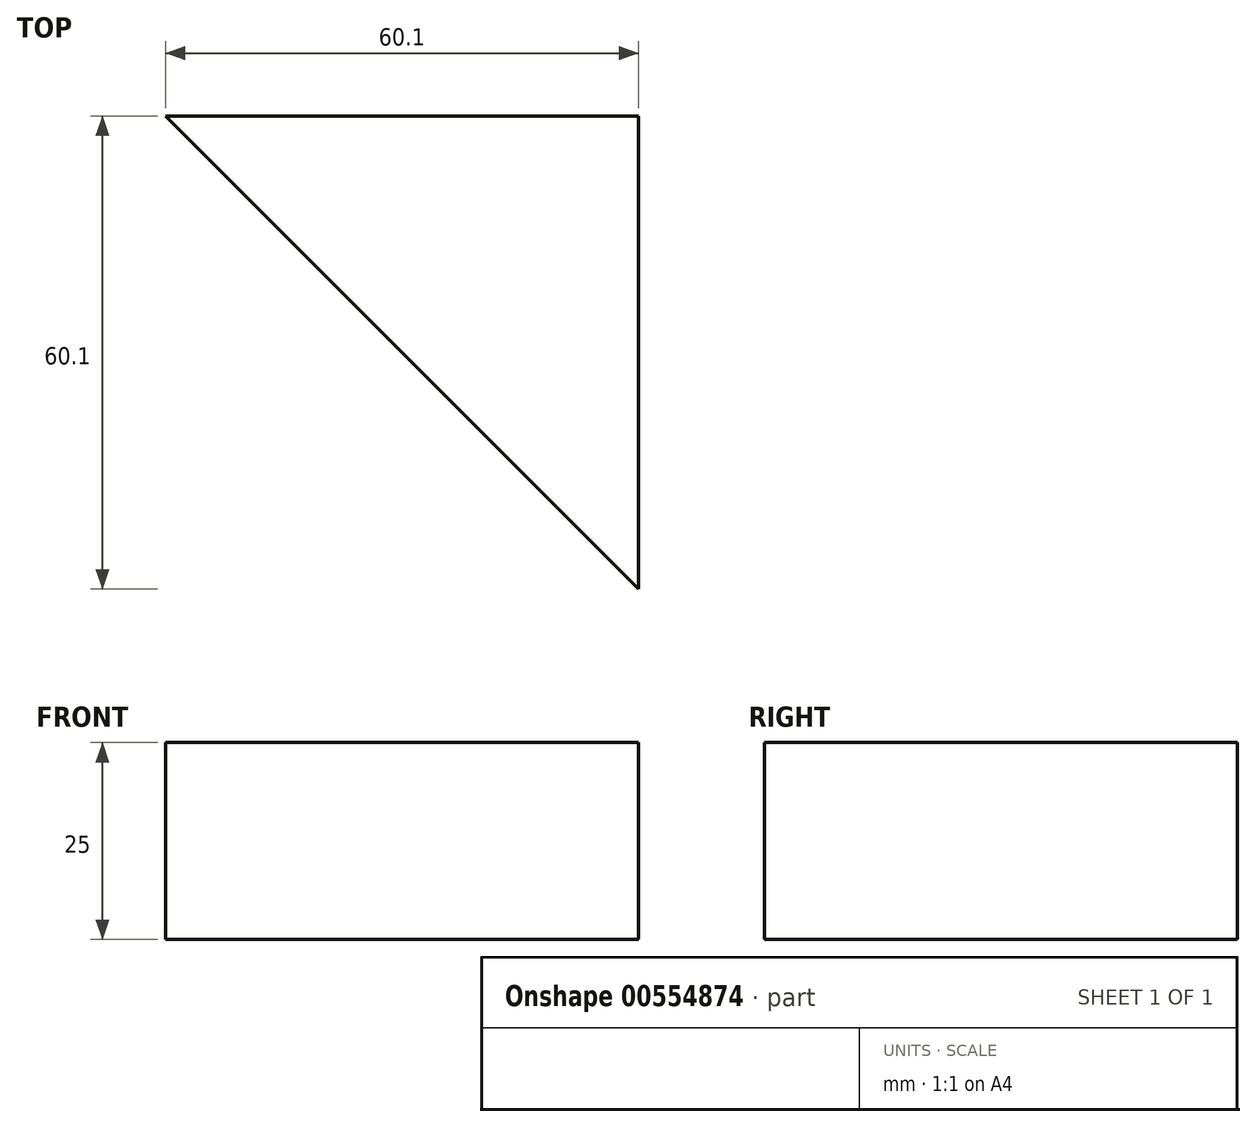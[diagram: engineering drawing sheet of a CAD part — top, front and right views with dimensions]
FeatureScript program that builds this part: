
annotation { "Feature Type Name" : "Feature", "Feature Type Description" : "" }
export const myFeature = defineFeature(function(context is Context, id is Id, definition is map)
    precondition{}
    {
        {
            var Q0;
            Q0=qCreatedBy(makeId("Top.planeOp"),FACE);
            var sketch = newSketch(context, id + "F0", { "sketchPlane" : qUnion([Q0])});
            skLineSegment(sketch, "E0", {"start": v(-42.37, 36.92) * mm, "end": v(17.73, -23.18) * mm});
            skLineSegment(sketch, "E1", {"start": v(-42.37, 36.92) * mm, "end": v(17.73, 36.92) * mm});
            skLineSegment(sketch, "E2", {"start": v(17.73, 36.92) * mm, "end": v(17.73, -23.18) * mm});
            skSolve(sketch);
        }
        {
            var Q0;
            Q0 = qSketchRegion(id + "F0", true);
            extrude(context, id + "F1", {"entities" : qUnion([Q0]), "depth" : 25 * mm, "offsetDistance" : 25 * mm});
        }
    });
